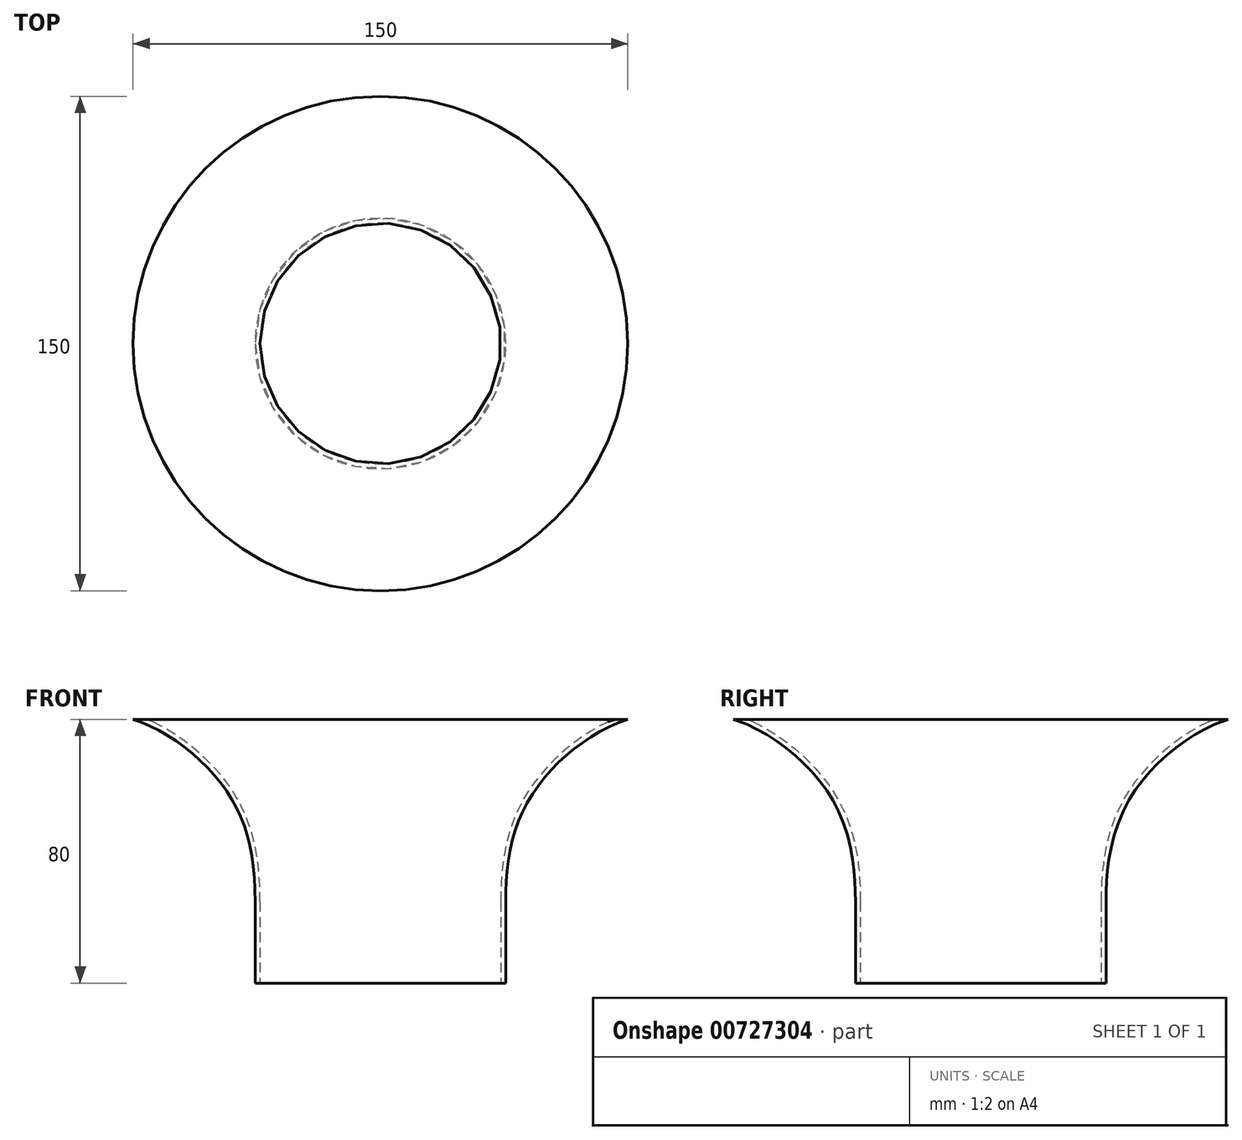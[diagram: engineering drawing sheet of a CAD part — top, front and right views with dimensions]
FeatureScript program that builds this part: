
annotation { "Feature Type Name" : "Feature", "Feature Type Description" : "" }
export const myFeature = defineFeature(function(context is Context, id is Id, definition is map)
    precondition{}
    {
        {
            var Q0;
            Q0=qCreatedBy(makeId("Front.planeOp"),FACE);
            var sketch = newSketch(context, id + "F0", { "sketchPlane" : qUnion([Q0])});
            skLineSegment(sketch, "E0", {"start": v(0, 0) * mm, "end": v(38, 0) * mm});
            skLineSegment(sketch, "E1", {"start": v(38, 0) * mm, "end": v(38, 24.6) * mm});
            skLineSegment(sketch, "E2", {"start": v(0, 0) * mm, "end": v(0, 80) * mm});
            skLineSegment(sketch, "E3", {"start": v(0, 80) * mm, "end": v(75, 80) * mm});
            skFitSpline(sketch, "E4", {"points": [v(38, 24.6) * mm, v(48, 60.17) * mm, v(75, 80) * mm], "startDerivative": vector(-0.42, 87.86) * mm, "endDerivative": vector(59.08, 18.52) * mm});
            skSolve(sketch);
        }
        {
            var Q0;
            Q0=makeQuery(id+"F0.imprint","IMPRINT",FACE,{"disambiguationData":[TD([[makeQuery(id+"F0.imprint","IMPRINT",EDGE,{"derivedFrom":sQuery(id+"F0.wireOp",EDGE,"E0")}),1.0]])]});
            var Q1;
            Q1=sQuery(id+"F0.wireOp",EDGE,"E2");
            revolve(context, id + "F1", {"surfaceOperationType" : NewSurfaceOperationType.NEW, "entities" : qUnion([Q0]), "axis" : qUnion([Q1]), "revolveType" : RevolveType.FULL});
        }
        {
            var Q0;
            Q0=makeQuery(id+"F1.opRevolve","SWEPT_FACE",FACE,{"disambiguationData":[OSD([sQuery(id+"F0.wireOp",EDGE,"E3")])]});
            var Q1;
            Q1=makeQuery(id+"F1.opRevolve","SWEPT_FACE",FACE,{"disambiguationData":[OSD([sQuery(id+"F0.wireOp",EDGE,"E0")])]});
            shell(context, id + "F2", {"entities" : qUnion([Q0, Q1]), "thickness" : 1.5 * mm});
        }
        {
            var Q0;
            Q0=makeQuery(id+"F2.opShell","OFFSET_EDGE",EDGE,{"disambiguationData":[OSD([sQuery(id+"F0.wireOp",EDGE,"E3"),sQuery(id+"F0.wireOp",EDGE,"E4")])]});
            fillet(context, id + "F3", {"entities" : qUnion([Q0]), "radius" : 8 * mm, "tangentPropagation" : true, "allowEdgeOverflow" : false});
        }
    });
